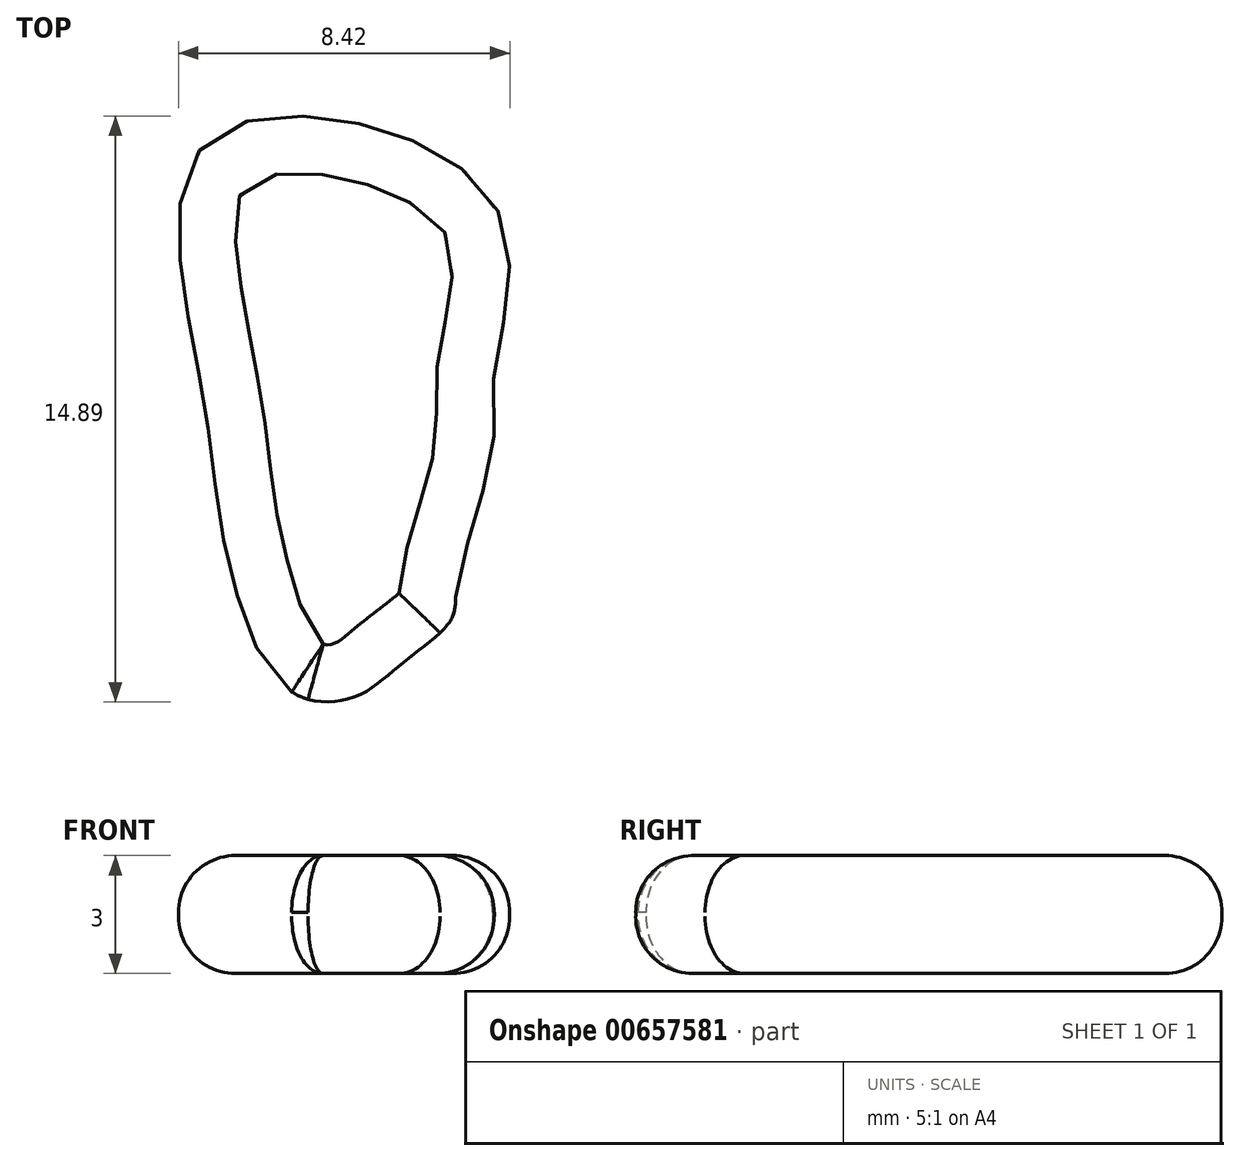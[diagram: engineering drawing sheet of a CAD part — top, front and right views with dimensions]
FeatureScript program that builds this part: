
annotation { "Feature Type Name" : "Feature", "Feature Type Description" : "" }
export const myFeature = defineFeature(function(context is Context, id is Id, definition is map)
    precondition{}
    {
        {
            var Q0;
            Q0=qCreatedBy(makeId("Top.planeOp"),FACE);
            var sketch = newSketch(context, id + "F0", { "sketchPlane" : qUnion([Q0])});
            skFitSpline(sketch, "E0", {"points": [v(-35.79, 31.64) * mm, v(-36.1, 25.59) * mm, v(-35.63, 22.24) * mm, v(-35.3, 20.64) * mm, v(-34.67, 18.73) * mm, v(-33.56, 17.46) * mm, v(-32.12, 17.46) * mm, v(-31, 18.25) * mm, v(-29.73, 19.37) * mm, v(-29.57, 20.17) * mm, v(-28.93, 22.56) * mm, v(-28.61, 24.15) * mm, v(-28.61, 25.75) * mm, v(-28.77, 30.2) * mm, v(-35.79, 31.64) * mm]});
            skSolve(sketch);
        }
        {
            var Q0;
            Q0 = qSketchRegion(id + "F0", true);
            extrude(context, id + "F1", {"entities" : qUnion([Q0]), "depth" : 3 * mm, "offsetDistance" : 25 * mm});
        }
        {
            var Q0;
            Q0=makeQuery(id+"F1.opExtrude","CAP_EDGE",EDGE,{"disambiguationData":[OSD([sQuery(id+"F0.wireOp",EDGE,"E0")])],"isStart":false});
            var Q1;
            Q1=makeQuery(id+"F1.opExtrude","CAP_EDGE",EDGE,{"disambiguationData":[OSD([sQuery(id+"F0.wireOp",EDGE,"E0")])],"isStart":true});
            fillet(context, id + "F2", {"entities" : qUnion([Q0, Q1]), "radius" : 1.45 * mm, "tangentPropagation" : true, "allowEdgeOverflow" : false});
        }
    });
